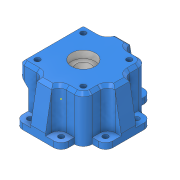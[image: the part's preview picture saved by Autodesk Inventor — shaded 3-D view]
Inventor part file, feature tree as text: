
AUTODESK INVENTOR PART (.ipt)
format: ipt  version: 2020 (Build 240168000, 168)  size: 645,632 bytes
history: native  units: in
note: dims shown in document units (in); Inventor stores cm internally (conversion verified against a paired STEP export)
features: sketch x33, extrude x32, mirror x5, fillet x4, chamfer x4, pattern_linear x3, pattern_circular x3, thicken_offset x2, other x1, plane x1
ambient origin geometry x8: Origin, YZ Plane, XZ Plane, XY Plane, X Axis, Y Axis, Z Axis, Center Point
bodies: Solid1 (feature_tree)
feature tree (88):
  extrude  "Extrusion1"  Depth=2.4016in
  extrude  "Extrusion2"  Depth=0.1575in
  fillet  "Fillet1"  Radius=1.2205in
  extrude  "Extrusion3"  Depth=0.1969in
  extrude  "Extrusion4"  Depth=0.1575in
  extrude  "Extrusion5"  Depth=0.1575in
  pattern_linear  "Rectangular Pattern1"  Count1=2 Spacing1=0.8268in
  other  "Work Axis1"
  pattern_circular  "Circular Pattern1"  Count=3 Angle=180.0deg
  extrude  "Extrusion7"  Depth=1.1811in
  pattern_circular  "Circular Pattern2"  Count=3 Angle=180.0deg
  extrude  "Extrusion8"  Depth=0.1969in
  extrude  "Extrusion9"  Depth=0.6732in
  extrude  "Extrusion10"  Depth=1.378in
  pattern_circular  "Circular Pattern3"  [2 undecoded]
  fillet  "Fillet2"  Radius=0.0787in
  extrude  "Extrusion11"  Depth=0.0787in
  extrude  "Extrusion12"  Depth=0.1969in TaperAngle=0.0deg
  extrude  "Extrusion13"  Depth=0.5512in
  extrude  "Extrusion14"  Depth=0.1181in TaperAngle=0.0deg
  plane  "Work Plane1"
  mirror  "Mirror1"
  extrude  "Extrusion15"  Depth=0.1575in TaperAngle=0.0deg
  thicken_offset  "Thicken1"
  extrude  "Extrusion16"  Depth=0.1969in TaperAngle=0.0deg
  extrude  "Extrusion17"  Depth=0.2362in TaperAngle=0.0deg
  sketch  "Sketch20"  dims[d51=1.5354in]
  extrude  "Extrusion19"  Depth=0.1969in
  extrude  "Extrusion20"  Depth=0.1969in
  chamfer  "Chamfer1"  Distance=0.315in
  chamfer  "Chamfer2"  Distance=0.1575in
  chamfer  "Chamfer3"  Angle=45.0deg  [1 undecoded]
  extrude  "Extrusion23"  Depth=0.0787in TaperAngle=0.0deg
  extrude  "Extrusion24"  Depth=0.1181in
  extrude  "Extrusion27"  Depth=0.1181in
  extrude  "Extrusion28"  Depth=0.1969in TaperAngle=0.0deg
  extrude  "Extrusion29"  Depth=0.1969in
  mirror  "Mirror2"
  extrude  "Extrusion30"  Depth=0.315in TaperAngle=0.0deg
  extrude  "Extrusion31"  Depth=0.1969in
  mirror  "Mirror3"
  extrude  "Extrusion32"  Depth=0.315in TaperAngle=0.0deg
  fillet  "Fillet6"  Radius=0.7874in
  mirror  "Mirror4"
  fillet  "Fillet7"  Radius=0.7874in
  sketch  "Sketch41"  dims[d67=0.315in]
  extrude  "Extrusion35"  Depth=0.0787in
  pattern_linear  "Rectangular Pattern6"  Spacing1=0.4724in  [1 undecoded]
  extrude  "Extrusion37"  Depth=0.3937in
  mirror  "Mirror6"
  extrude  "Extrusion38"  Depth=0.4724in TaperAngle=0.0deg
  pattern_linear  "Rectangular Pattern7"  Spacing1=0.6289in  [1 undecoded]
  chamfer  "Chamfer6"  Distance=0.1969in
  extrude  "Extrusion39"  Depth=0.1969in
  extrude  "Extrusion40"  Depth=0.1969in
  extrude  "Extrusion41"  [1 undecoded]
  thicken_offset  "Thicken2"
  sketch  "Sketch1"  dims[d0=1.2205in d1=2.4016in]
  sketch  "Sketch2"  dims[d2=0.1575in d3=0.0in d4=0.5906in d5=1.2205in]
  sketch  "Sketch3"  dims[d6=0.1575in d7=0.0in d8=0.1969in]
  sketch  "Sketch4"  dims[d9=0.1575in d10=0.0in d11=1.378in]
  sketch  "Sketch5"  dims[d12=0.1575in d13=0.0in d14=0.1417in]
  sketch  "Sketch7"  dims[d15=0.1575in d16=0.0in d17=0.7874in d19=0.8268in d22=1.1811in d23=180.0deg]
  sketch  "Sketch8"  dims[d25=0.7874in d26=0.0in d27=1.1811in d28=-1.2368in]
  sketch  "Sketch9"  dims[d30=0.4724in d31=0.0in]
  sketch  "Sketch10"  dims[d33=0.2362in]
  sketch  "Sketch11"  dims[d34=1.2205in]
  sketch  "Sketch12"  dims[d35=0.4724in d36=0.0in]
  sketch  "Sketch13"  dims[d37=0.3937in]
  sketch  "Sketch14"  dims[d38=1.2598in d39=0.0in d40=1.1811in d41=180.0deg]
  sketch  "Sketch15"  dims[d43=0.1969in d44=1.7717in]
  sketch  "Sketch16"  dims[d45=0.9449in d46=0.0in d47=0.6732in]
  sketch  "Sketch18"  dims[d48=0.9449in d49=0.0in d50=1.378in]
  sketch  "Sketch21"  dims[d52=0.9449in d53=0.0in]
  sketch  "Sketch24"  dims[d55=1.4173in d56=0.0in]
  sketch  "Sketch25"  dims[d57=0.4724in]
  sketch  "Sketch28"  dims[d58=1.5354in]
  sketch  "Sketch30"  dims[d59=0.4724in d60=0.0in]
  sketch  "Sketch31"  dims[d61=0.1969in]
  sketch  "Sketch32"  dims[d62=0.1969in]
  sketch  "Sketch33"  dims[d63=0.1969in d64=0.0in]
  sketch  "Sketch35"  dims[d66=0.315in]
  sketch  "Sketch42"  dims[d68=0.315in d69=0.0in]
  sketch  "Sketch46"  dims[d73=0.1417in]
  sketch  "Sketch48"  dims[d76=1.7717in]
  sketch  "Sketch49"  dims[d77=0.9843in]
  sketch  "Sketch50"  dims[d78=0.1575in d79=0.0in]
  sketch  "Sketch51"  dims[d80=0.315in d81=0.0in d107=0.1772in d108=0.0787in d109=0.5497in d110=0.1772in d111=0.0787in d112=0.5497in d113=0.1772in d114=0.0787in d115=0.5497in d119=0.0591in d120=0.0in d121=0.5512in d122=0.1181in d123=0.0in d130=0.1575in d131=0.0787in d132=0.0in d133=0.0in d135=0.8465in d136=0.0in d137=0.2362in d138=0.0in d139=0.6102in d140=0.1417in d141=0.315in d142=0.0in d150=0.1575in d151=0.0in d152=45.0deg d153=0.0787in d154=0.0in d161=0.1181in d162=0.1181in d164=0.0984in d165=0.0in d166=0.7874in d168=1.2205in d169=0.7874in d171=1.2205in d180=0.315in d181=0.0in d182=0.1417in d183=0.315in d184=0.0in d185=0.7874in d187=1.2205in d188=0.7874in d190=1.2205in d191=0.0787in d192=0.0787in d193=0.5497in d194=0.4724in d195=0.0in d196=0.3937in d197=0.4724in d198=0.0in d199=0.6289in d200=0.1969in d201=0.0in d202=0.0591in d203=0.0591in]
note: 6 required parameter values undecoded (feature->parameter linkage not recoverable at this tier; creation-order binding heuristic only, values carry confidence <= 0.55)
